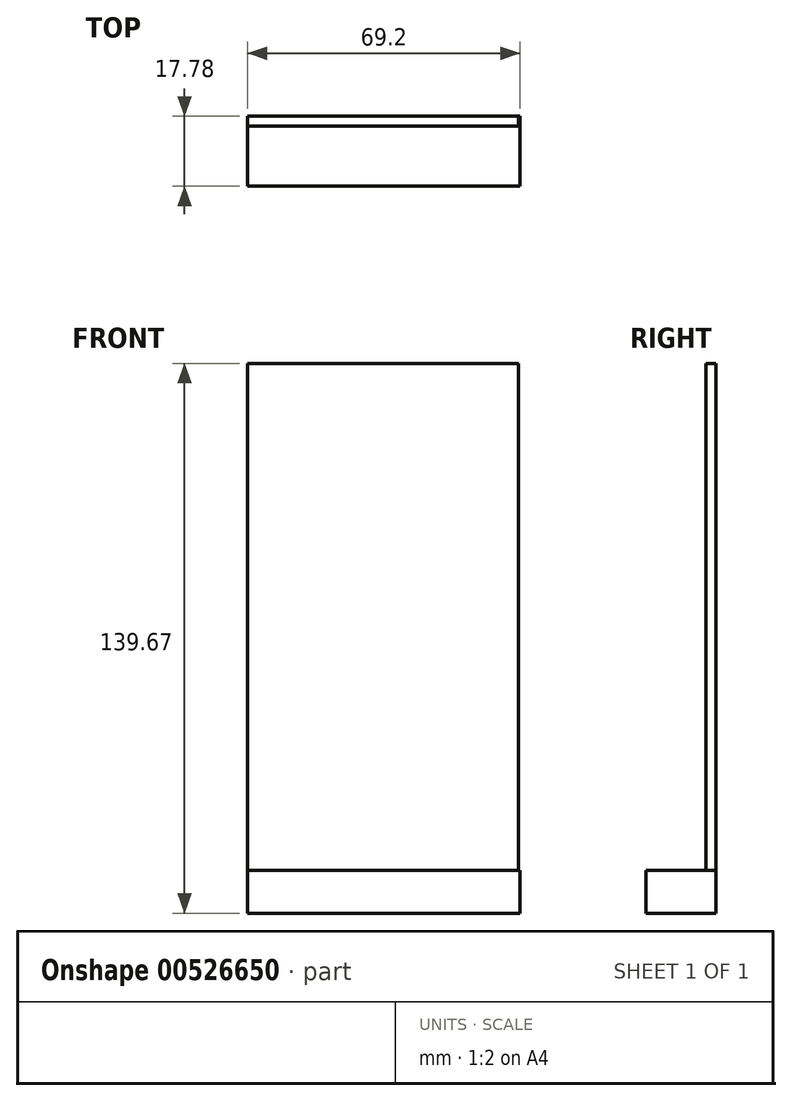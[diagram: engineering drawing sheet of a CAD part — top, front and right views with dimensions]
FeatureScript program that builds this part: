
annotation { "Feature Type Name" : "Feature", "Feature Type Description" : "" }
export const myFeature = defineFeature(function(context is Context, id is Id, definition is map)
    precondition{}
    {
        {
            var Q0;
            Q0=qCreatedBy(makeId("Front.planeOp"),FACE);
            var sketch = newSketch(context, id + "F0", { "sketchPlane" : qUnion([Q0])});
            skLineSegment(sketch, "E0.bottom", {"start": v(-34.4, 64.38) * mm, "end": v(34.4, 64.38) * mm});
            skLineSegment(sketch, "E0.top", {"start": v(-34.4, -64.38) * mm, "end": v(34.4, -64.38) * mm});
            skLineSegment(sketch, "E0.left", {"start": v(-34.4, 64.38) * mm, "end": v(-34.4, -64.38) * mm});
            skLineSegment(sketch, "E0.right", {"start": v(34.4, 64.38) * mm, "end": v(34.4, -64.38) * mm});
            skPoint(sketch, "E0.middle", {"position": v(0, 0) * mm});
            skLineSegment(sketch, "E1.bottom", {"start": v(-34.4, -64.38) * mm, "end": v(34.81, -64.38) * mm});
            skLineSegment(sketch, "E1.top", {"start": v(-34.4, -75.29) * mm, "end": v(34.81, -75.29) * mm});
            skLineSegment(sketch, "E1.left", {"start": v(-34.4, -64.38) * mm, "end": v(-34.4, -75.29) * mm});
            skLineSegment(sketch, "E1.right", {"start": v(34.81, -64.38) * mm, "end": v(34.81, -75.29) * mm});
            skSolve(sketch);
        }
        {
            var Q0;
            Q0=makeQuery(id+"F0.imprint","IMPRINT",FACE,{"disambiguationData":[TD([[makeQuery(id+"F0.imprint","IMPRINT",EDGE,{"derivedFrom":sQuery(id+"F0.wireOp",EDGE,"E0.bottom")}),-1.0]])]});
            extrude(context, id + "F1", {"entities" : qUnion([Q0]), "depth" : 2.54 * mm, "offsetDistance" : 25.4 * mm});
        }
        {
            var Q0;
            Q0=makeQuery(id+"F0.imprint","IMPRINT",FACE,{"disambiguationData":[TD([[makeQuery(id+"F0.imprint","IMPRINT",EDGE,{"derivedFrom":sQuery(id+"F0.wireOp",EDGE,"E1.top")}),1.0]])]});
            extrude(context, id + "F2", {"entities" : qUnion([Q0]), "operationType" : NewBodyOperationType.ADD, "depth" : 17.78 * mm, "offsetDistance" : 25.4 * mm});
        }
    });
